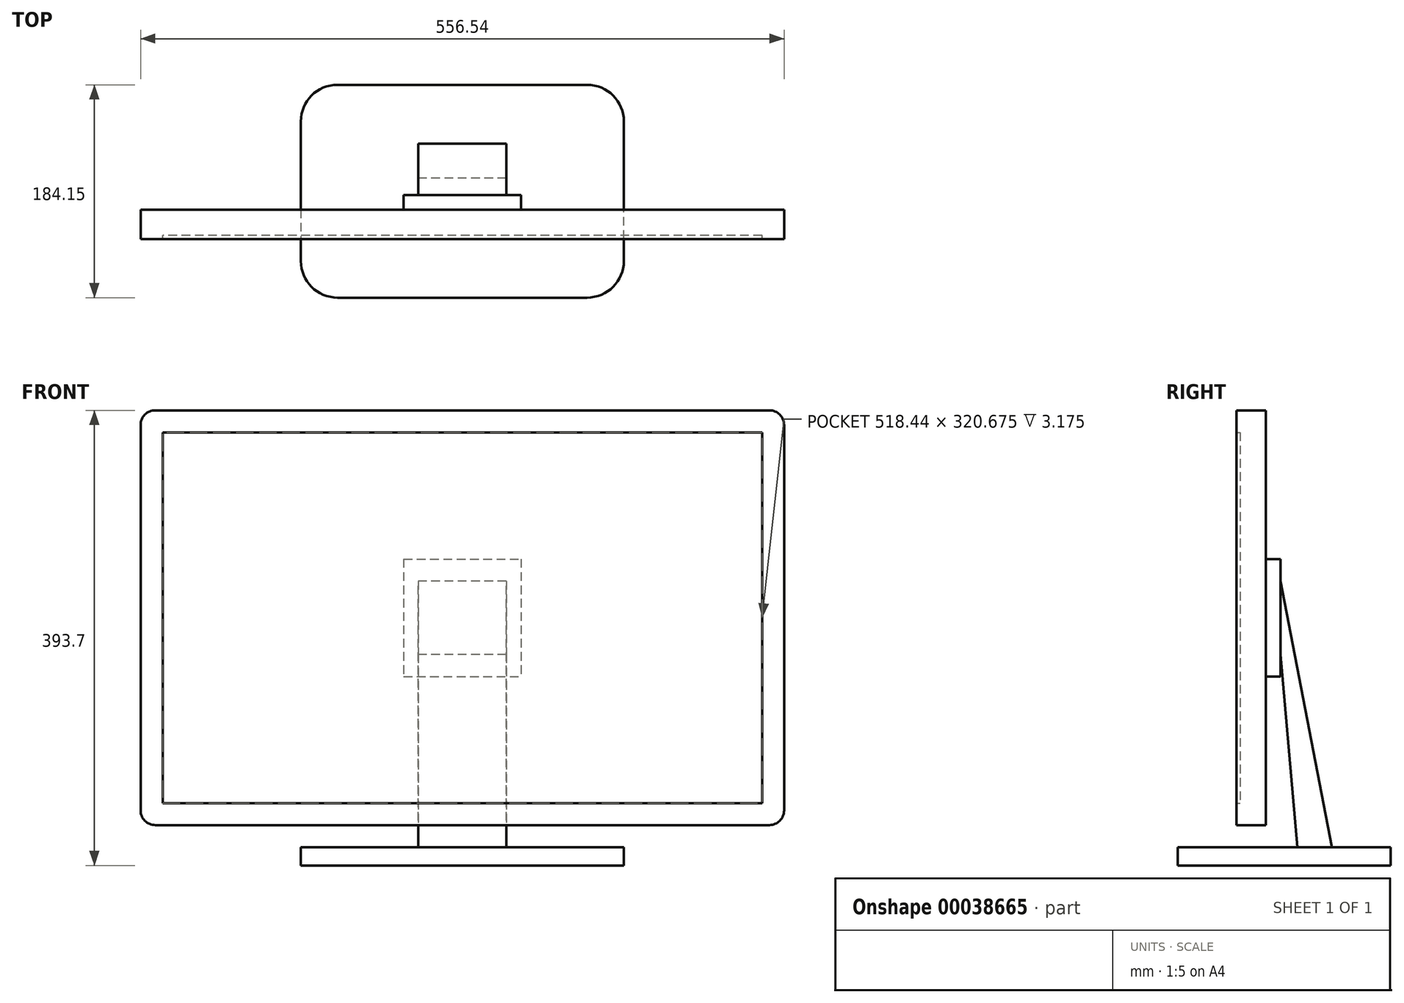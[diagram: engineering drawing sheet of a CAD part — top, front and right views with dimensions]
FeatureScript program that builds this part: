
annotation { "Feature Type Name" : "Feature", "Feature Type Description" : "" }
export const myFeature = defineFeature(function(context is Context, id is Id, definition is map)
    precondition{}
    {
        {
            var Q0;
            Q0=qCreatedBy(makeId("Front.planeOp"),FACE);
            var sketch = newSketch(context, id + "F0", { "sketchPlane" : qUnion([Q0])});
            skLineSegment(sketch, "E0.rect.bottom", {"start": v(259.22, 160.34) * mm, "end": v(-259.22, 160.34) * mm});
            skLineSegment(sketch, "E0.rect.top", {"start": v(259.22, -160.34) * mm, "end": v(-259.22, -160.34) * mm});
            skLineSegment(sketch, "E0.rect.left", {"start": v(259.22, 160.34) * mm, "end": v(259.22, -160.34) * mm});
            skLineSegment(sketch, "E0.rect.right", {"start": v(-259.22, 160.34) * mm, "end": v(-259.22, -160.34) * mm});
            skPoint(sketch, "E0.rect.middle", {"position": v(0, 0) * mm});
            skLineSegment(sketch, "E1", {"start": v(-259.22, 160.34) * mm, "end": v(259.22, -160.34) * mm, "construction": true});
            skLineSegment(sketch, "E2.0", {"start": v(278.27, 166.69) * mm, "end": v(278.27, -166.69) * mm});
            skLineSegment(sketch, "E2.1", {"start": v(265.57, 179.39) * mm, "end": v(-265.57, 179.39) * mm});
            skLineSegment(sketch, "E2.2", {"start": v(-278.27, 166.69) * mm, "end": v(-278.27, -166.69) * mm});
            skLineSegment(sketch, "E2.3", {"start": v(265.57, -179.39) * mm, "end": v(-265.57, -179.39) * mm});
            skPoint(sketch, "E3.visualSharp", {"position": v(-278.27, 179.39) * mm});
            skArc(sketch, "E3.filletArc", {"start": v(-265.57, 179.39) * mm, "mid": v(-274.55, 175.67) * mm, "end": v(-278.27, 166.69) * mm});
            skPoint(sketch, "E4.visualSharp", {"position": v(278.27, 179.39) * mm});
            skArc(sketch, "E4.filletArc", {"start": v(278.27, 166.69) * mm, "mid": v(274.55, 175.67) * mm, "end": v(265.57, 179.39) * mm});
            skPoint(sketch, "E5.visualSharp", {"position": v(278.27, -179.39) * mm});
            skArc(sketch, "E5.filletArc", {"start": v(265.57, -179.39) * mm, "mid": v(274.55, -175.67) * mm, "end": v(278.27, -166.69) * mm});
            skPoint(sketch, "E6.visualSharp", {"position": v(-278.27, -179.39) * mm});
            skArc(sketch, "E6.filletArc", {"start": v(-278.27, -166.69) * mm, "mid": v(-274.55, -175.67) * mm, "end": v(-265.57, -179.39) * mm});
            skSolve(sketch);
        }
        {
            var Q0;
            Q0=makeQuery(id+"F0.imprint","IMPRINT",FACE,{"disambiguationData":[TD([[makeQuery(id+"F0.imprint","IMPRINT",EDGE,{"derivedFrom":sQuery(id+"F0.wireOp",EDGE,"E0.rect.bottom")}),-1.0]])]});
            extrude(context, id + "F1", {"entities" : qUnion([Q0]), "depth" : 25.4 * mm});
        }
        {
            var Q0;
            Q0=makeQuery(id+"F0.imprint","IMPRINT",FACE,{"disambiguationData":[TD([[makeQuery(id+"F0.imprint","IMPRINT",EDGE,{"derivedFrom":sQuery(id+"F0.wireOp",EDGE,"E0.rect.bottom")}),1.0]])]});
            var Q1;
            Q1=sQuery(id+"F0.wireOp",EDGE,"E0.rect.bottom");
            var Q2;
            Q2=sQuery(id+"F0.wireOp",EDGE,"E0.rect.right");
            var Q3;
            Q3=sQuery(id+"F0.wireOp",EDGE,"E0.rect.top");
            var Q4;
            Q4=sQuery(id+"F0.wireOp",EDGE,"E0.rect.left");
            extrude(context, id + "F2", {"entities" : qUnion([Q0]), "operationType" : NewBodyOperationType.ADD, "surfaceEntities" : qUnion([Q1, Q2, Q3, Q4]), "depth" : 22.22 * mm});
        }
        {
            var Q0;
            Q0=makeQuery(id+"F0.imprint","IMPRINT",FACE,{"disambiguationData":[TD([[makeQuery(id+"F0.imprint","IMPRINT",EDGE,{"derivedFrom":sQuery(id+"F0.wireOp",EDGE,"E0.rect.bottom")}),1.0]])]});
            var sketch = newSketch(context, id + "F3", { "sketchPlane" : qUnion([Q0])});
            skLineSegment(sketch, "E7.rect.bottom", {"start": v(-50.8, 50.8) * mm, "end": v(50.8, 50.8) * mm});
            skLineSegment(sketch, "E7.rect.top", {"start": v(-50.8, -50.8) * mm, "end": v(50.8, -50.8) * mm});
            skLineSegment(sketch, "E7.rect.left", {"start": v(-50.8, 50.8) * mm, "end": v(-50.8, -50.8) * mm});
            skLineSegment(sketch, "E7.rect.right", {"start": v(50.8, 50.8) * mm, "end": v(50.8, -50.8) * mm});
            skPoint(sketch, "E7.rect.middle", {"position": v(0, 0) * mm});
            skSolve(sketch);
        }
        {
            var Q0;
            Q0 = qSketchRegion(id + "F3", true);
            extrude(context, id + "F4", {"entities" : qUnion([Q0]), "operationType" : NewBodyOperationType.ADD, "oppositeDirection" : true, "depth" : 12.7 * mm});
        }
        {
            var Q0;
            Q0=qCreatedBy(makeId("Right.planeOp"),FACE);
            var sketch = newSketch(context, id + "F5", { "sketchPlane" : qUnion([Q0])});
            skLineSegment(sketch, "E8", {"start": v(12.7, -31.75) * mm, "end": v(27.28, -198.44) * mm});
            skLineSegment(sketch, "E9", {"start": v(27.28, -198.44) * mm, "end": v(-76.2, -198.44) * mm});
            skLineSegment(sketch, "E10", {"start": v(-76.2, -198.44) * mm, "end": v(-76.2, -214.31) * mm});
            skLineSegment(sketch, "E11", {"start": v(-76.2, -214.31) * mm, "end": v(107.95, -214.31) * mm});
            skLineSegment(sketch, "E12", {"start": v(107.95, -214.31) * mm, "end": v(107.95, -198.44) * mm});
            skLineSegment(sketch, "E13", {"start": v(107.95, -198.44) * mm, "end": v(57.15, -198.44) * mm});
            skLineSegment(sketch, "E14", {"start": v(57.15, -198.44) * mm, "end": v(12.7, 31.75) * mm});
            skLineSegment(sketch, "E15", {"start": v(12.7, 31.75) * mm, "end": v(12.7, -31.75) * mm});
            skSolve(sketch);
        }
        {
            var Q0;
            Q0 = qSketchRegion(id + "F5", true);
            extrude(context, id + "F6", {"entities" : qUnion([Q0]), "operationType" : NewBodyOperationType.ADD, "endBound" : BoundingType.SYMMETRIC, "depth" : 76.2 * mm});
        }
        {
            var Q0;
            Q0=makeQuery(id+"F6.opExtrude","CAP_FACE",FACE,{"disambiguationData":[OSD([sQuery(id+"F5.wireOp",EDGE,"E8"),sQuery(id+"F5.wireOp",EDGE,"E9"),sQuery(id+"F5.wireOp",EDGE,"E10"),sQuery(id+"F5.wireOp",EDGE,"E11"),sQuery(id+"F5.wireOp",EDGE,"E12"),sQuery(id+"F5.wireOp",EDGE,"E13"),sQuery(id+"F5.wireOp",EDGE,"E14"),sQuery(id+"F5.wireOp",EDGE,"E15")])],"isStart":false});
            var sketch = newSketch(context, id + "F7", { "sketchPlane" : qUnion([Q0])});
            skLineSegment(sketch, "E16.bottom", {"start": v(-76.2, -198.44) * mm, "end": v(107.95, -198.44) * mm});
            skLineSegment(sketch, "E16.top", {"start": v(-76.2, -214.31) * mm, "end": v(107.95, -214.31) * mm});
            skLineSegment(sketch, "E16.left", {"start": v(-76.2, -198.44) * mm, "end": v(-76.2, -214.31) * mm});
            skLineSegment(sketch, "E16.right", {"start": v(107.95, -198.44) * mm, "end": v(107.95, -214.31) * mm});
            skSolve(sketch);
        }
        {
            var Q0;
            Q0 = qSketchRegion(id + "F7", true);
            extrude(context, id + "F8", {"entities" : qUnion([Q0]), "operationType" : NewBodyOperationType.ADD, "depth" : 101.6 * mm});
        }
        {
            var Q0;
            Q0=makeQuery(id+"F6.opExtrude","CAP_FACE",FACE,{"disambiguationData":[OSD([sQuery(id+"F5.wireOp",EDGE,"E8"),sQuery(id+"F5.wireOp",EDGE,"E9"),sQuery(id+"F5.wireOp",EDGE,"E10"),sQuery(id+"F5.wireOp",EDGE,"E11"),sQuery(id+"F5.wireOp",EDGE,"E12"),sQuery(id+"F5.wireOp",EDGE,"E13"),sQuery(id+"F5.wireOp",EDGE,"E14"),sQuery(id+"F5.wireOp",EDGE,"E15")])],"isStart":true});
            var sketch = newSketch(context, id + "F9", { "sketchPlane" : qUnion([Q0])});
            skLineSegment(sketch, "E17.bottom", {"start": v(-107.95, -198.44) * mm, "end": v(76.2, -198.44) * mm});
            skLineSegment(sketch, "E17.top", {"start": v(-107.95, -214.31) * mm, "end": v(76.2, -214.31) * mm});
            skLineSegment(sketch, "E17.left", {"start": v(-107.95, -198.44) * mm, "end": v(-107.95, -214.31) * mm});
            skLineSegment(sketch, "E17.right", {"start": v(76.2, -198.44) * mm, "end": v(76.2, -214.31) * mm});
            skSolve(sketch);
        }
        {
            var Q0;
            Q0 = qSketchRegion(id + "F9", true);
            extrude(context, id + "F10", {"entities" : qUnion([Q0]), "operationType" : NewBodyOperationType.ADD, "depth" : 101.6 * mm});
        }
        {
            var Q0;
            Q0=makeQuery(id+"F10.opExtrude","CAP_EDGE",EDGE,{"disambiguationData":[OSD([sQuery(id+"F9.wireOp",EDGE,"E17.left")])],"isStart":false});
            var Q1;
            Q1=makeQuery(id+"F8.opExtrude","CAP_EDGE",EDGE,{"disambiguationData":[OSD([sQuery(id+"F7.wireOp",EDGE,"E16.right")])],"isStart":false});
            var Q2;
            Q2=makeQuery(id+"F8.opExtrude","CAP_EDGE",EDGE,{"disambiguationData":[OSD([sQuery(id+"F7.wireOp",EDGE,"E16.left")])],"isStart":false});
            var Q3;
            Q3=makeQuery(id+"F10.opExtrude","CAP_EDGE",EDGE,{"disambiguationData":[OSD([sQuery(id+"F9.wireOp",EDGE,"E17.right")])],"isStart":false});
            fillet(context, id + "F11", {"entities" : qUnion([Q0, Q1, Q2, Q3]), "radius" : 31.75 * mm, "tangentPropagation" : true, "allowEdgeOverflow" : false});
        }
    });
